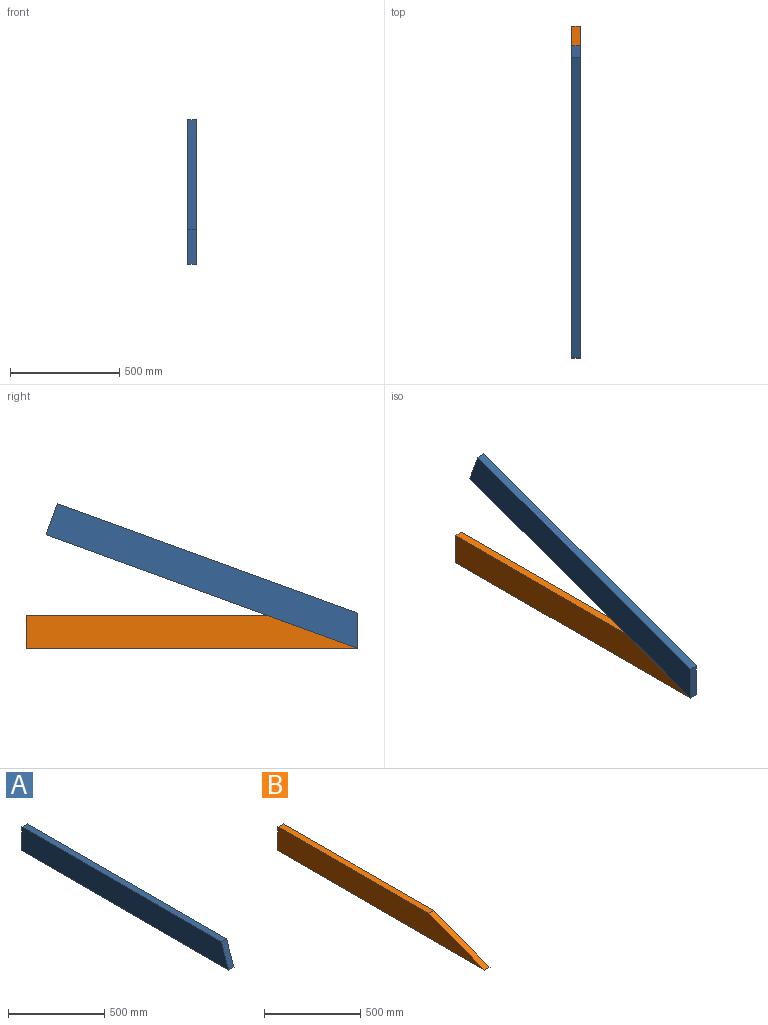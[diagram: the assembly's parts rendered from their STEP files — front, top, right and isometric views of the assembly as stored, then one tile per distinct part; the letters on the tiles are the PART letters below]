
ASSEMBLY  parts=2 mates=1
PART A: 6 faces, bbox 38x1520x152 mm
  f0: plane 1464.68x38mm, normal (0,0,1), area 55657.7mm2, adj f1,f2,f3,f5
  f1: plane 152x38mm, normal (0,1,0), area 5776mm2, adj f0,f2,f3,f4
  f2: plane 1520x152mm, normal (-1,0,0), area 226835.4mm2, adj f0,f1,f4,f5
  f3: plane 1520x152mm, normal (1,0,0), area 226835.4mm2, adj f0,f1,f4,f5
  f4: plane 1520x38mm, normal (0,0,-1), area 57760mm2, adj f1,f2,f3,f5
  f5: plane 152x55.32mm, normal (0,-0.94,0.34), area 6146.7mm2, adj f0,f2,f3,f4
PART B: 6 faces, bbox 38x1520x152 mm
  f0: plane 1102.38x38mm, normal (0,0,1), area 41890.6mm2, adj f1,f2,f3,f5
  f1: plane 152x38mm, normal (0,1,0), area 5776mm2, adj f0,f2,f3,f4
  f2: plane 1520x152mm, normal (-1,0,0), area 199301.1mm2, adj f0,f1,f4,f5
  f3: plane 1520x152mm, normal (1,0,0), area 199301.1mm2, adj f0,f1,f4,f5
  f4: plane 1520x38mm, normal (0,0,-1), area 57760mm2, adj f1,f2,f3,f5
  f5: plane 417.62x152mm, normal (0,-0.34,0.94), area 16887.9mm2, adj f0,f2,f3,f4
PLACE A rot(axis=(1,0,0),20deg) t=(-19,395.28,1.49)mm
PLACE B t=(-19,486.94,-518.38)mm
MATE fastened A.f4 <-> B.f5  axis (0,0.34,-0.94) through (0,-1033.06,-518.38)mm
